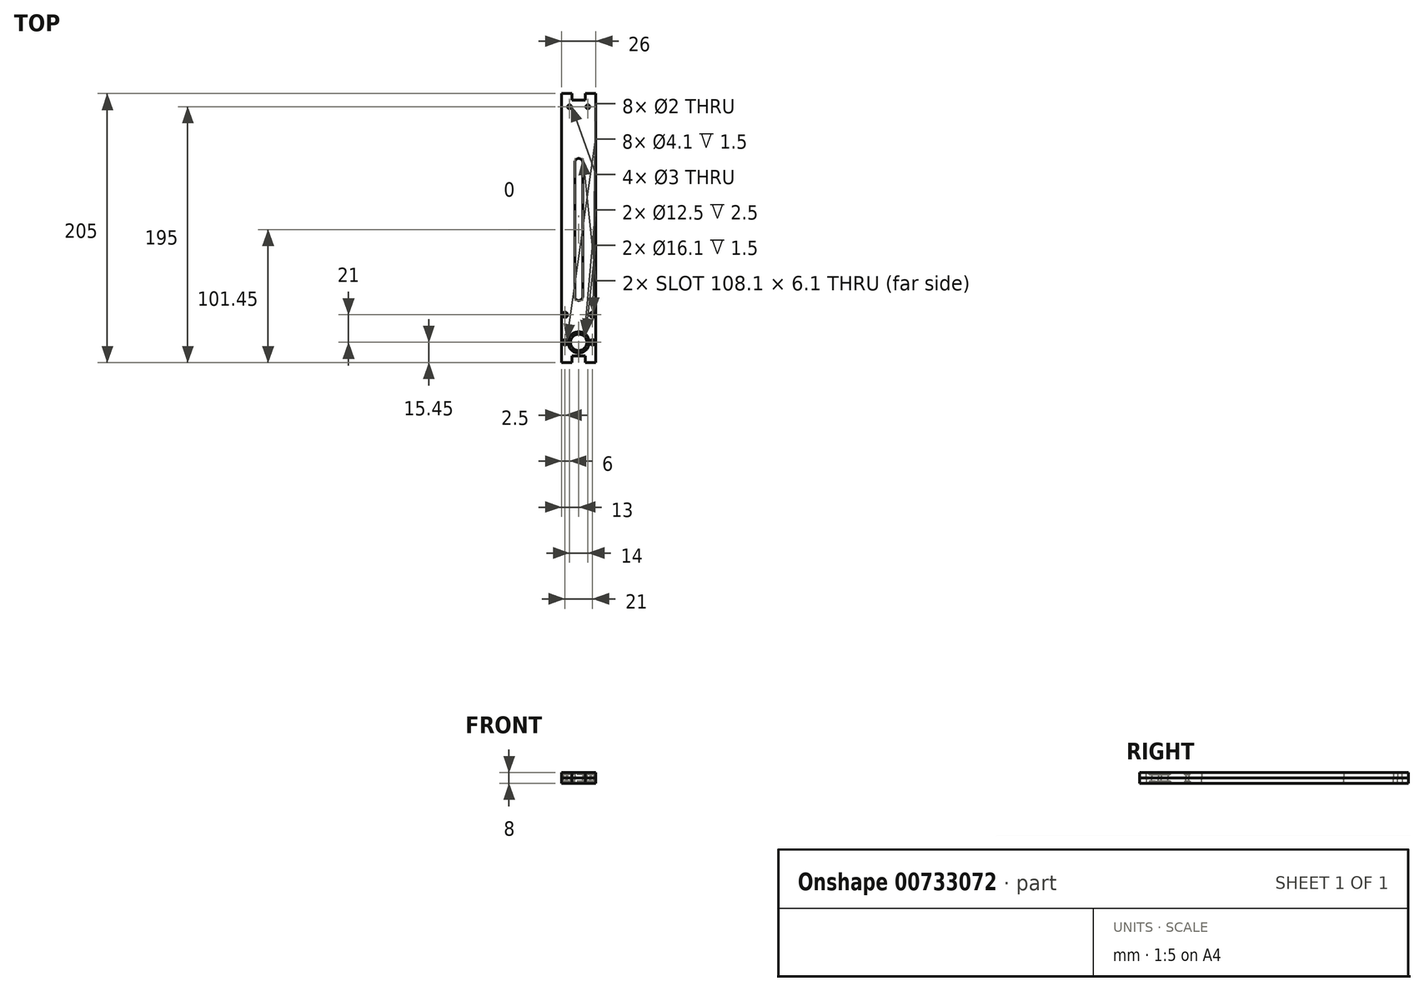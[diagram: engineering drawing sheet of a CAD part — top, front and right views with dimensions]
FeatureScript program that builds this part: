
annotation { "Feature Type Name" : "Feature", "Feature Type Description" : "" }
export const myFeature = defineFeature(function(context is Context, id is Id, definition is map)
    precondition{}
    {
        {
            var Q0;
            Q0=qCreatedBy(makeId("Top.planeOp"),FACE);
            var sketch = newSketch(context, id + "F0", { "sketchPlane" : qUnion([Q0])});
            skArc(sketch, "E0", {"start": v(3.05, 51) * mm, "mid": v(0, 54.05) * mm, "end": v(-3.05, 51) * mm});
            skArc(sketch, "E1.MirrorC", {"start": v(3.05, -51) * mm, "mid": v(0, -54.05) * mm, "end": v(-3.05, -51) * mm});
            skLineSegment(sketch, "E2", {"start": v(-3.05, 51) * mm, "end": v(-3.05, -51) * mm});
            skLineSegment(sketch, "E3.MirrorCS", {"start": v(3.05, 51) * mm, "end": v(3.05, -51) * mm});
            skCircle(sketch, "E4", {"center": v(-10.5, -65) * mm, "radius": 1 * mm});
            skCircle(sketch, "E5.MirrorC", {"center": v(10.5, -65) * mm, "radius": 1 * mm});
            skCircle(sketch, "E6", {"center": v(-10.5, -86) * mm, "radius": 1 * mm});
            skCircle(sketch, "E7.MirrorC", {"center": v(10.5, -86) * mm, "radius": 1 * mm});
            skArc(sketch, "E8", {"start": v(6.25, -86) * mm, "mid": v(0, -79.75) * mm, "end": v(-6.25, -86) * mm});
            skLineSegment(sketch, "E9", {"start": v(-6.25, -101.45) * mm, "end": v(-13, -101.45) * mm});
            skLineSegment(sketch, "E10", {"start": v(-13, -101.45) * mm, "end": v(-13, 98.55) * mm});
            skPoint(sketch, "E11", {"position": v(0, -92.25) * mm});
            skLineSegment(sketch, "E12", {"start": v(-13, 98.55) * mm, "end": v(0, 98.55) * mm});
            skLineSegment(sketch, "E13.MirrorCS", {"start": v(13, 98.55) * mm, "end": v(0, 98.55) * mm});
            skLineSegment(sketch, "E14.MirrorCS", {"start": v(13, -101.45) * mm, "end": v(13, 98.55) * mm});
            skLineSegment(sketch, "E15.MirrorCS", {"start": v(6.25, -101.45) * mm, "end": v(13, -101.45) * mm});
            skLineSegment(sketch, "E16", {"start": v(-6.25, -86) * mm, "end": v(-6.25, -101.45) * mm});
            skLineSegment(sketch, "E17.MirrorCS", {"start": v(6.25, -86) * mm, "end": v(6.25, -101.45) * mm});
            skPoint(sketch, "E18.orphan", {"position": v(0, -101.45) * mm});
            skPoint(sketch, "E19", {"position": v(0, -54.05) * mm});
            skPoint(sketch, "E20", {"position": v(0, 54.05) * mm});
            skCircle(sketch, "E21", {"center": v(-7, 93.55) * mm, "radius": 1.5 * mm});
            skCircle(sketch, "E22.MirrorC", {"center": v(7, 93.55) * mm, "radius": 1.5 * mm});
            skArc(sketch, "E23", {"start": v(-6.25, -86) * mm, "mid": v(0, -92.25) * mm, "end": v(6.25, -86) * mm});
            skLineSegment(sketch, "E24", {"start": v(-6.25, -101.45) * mm, "end": v(6.25, -101.45) * mm});
            skSolve(sketch);
        }
        {
            var Q0;
            Q0=qSketchRegion(id+"F0",true);
            extrude(context, id + "F1", {"entities" : qUnion([Q0]), "depth" : 4 * mm, "offsetDistance" : 25 * mm});
        }
        {
            var Q0;
            Q0=makeQuery(id+"F1.opExtrude","CAP_FACE",FACE,{"disambiguationData":[OSD([sQuery(id+"F0.wireOp",EDGE,"E0"),sQuery(id+"F0.wireOp",EDGE,"E1.MirrorC"),sQuery(id+"F0.wireOp",EDGE,"E2"),sQuery(id+"F0.wireOp",EDGE,"E3.MirrorCS"),sQuery(id+"F0.wireOp",EDGE,"E4"),sQuery(id+"F0.wireOp",EDGE,"E5.MirrorC"),sQuery(id+"F0.wireOp",EDGE,"E6"),sQuery(id+"F0.wireOp",EDGE,"E7.MirrorC"),sQuery(id+"F0.wireOp",EDGE,"E8"),sQuery(id+"F0.wireOp",EDGE,"E9"),sQuery(id+"F0.wireOp",EDGE,"E10"),sQuery(id+"F0.wireOp",EDGE,"E12"),sQuery(id+"F0.wireOp",EDGE,"E13.MirrorCS"),sQuery(id+"F0.wireOp",EDGE,"E14.MirrorCS"),sQuery(id+"F0.wireOp",EDGE,"E15.MirrorCS"),sQuery(id+"F0.wireOp",EDGE,"E16"),sQuery(id+"F0.wireOp",EDGE,"E17.MirrorCS")])],"isStart":false});
            var sketch = newSketch(context, id + "F2", { "sketchPlane" : qUnion([Q0])});
            skCircle(sketch, "E25", {"center": v(0, -86) * mm, "radius": 8.05 * mm});
            skCircle(sketch, "E26", {"center": v(-10.5, -86) * mm, "radius": 2.05 * mm});
            skCircle(sketch, "E27", {"center": v(-10.5, -65) * mm, "radius": 2.05 * mm});
            skCircle(sketch, "E28.MirrorC", {"center": v(10.5, -65) * mm, "radius": 2.05 * mm});
            skCircle(sketch, "E29.MirrorC", {"center": v(10.5, -86) * mm, "radius": 2.05 * mm});
            skSolve(sketch);
        }
        {
            var Q0;
            Q0=qSketchRegion(id+"F2",true);
            extrude(context, id + "F3", {"entities" : qUnion([Q0]), "operationType" : NewBodyOperationType.REMOVE, "oppositeDirection" : true, "depth" : 1.5 * mm, "offsetDistance" : 25 * mm});
        }
        {
            var Q0;
            Q0=makeQuery(id+"F1.opExtrude","CAP_FACE",FACE,{"disambiguationData":[OSD([sQuery(id+"F0.wireOp",EDGE,"E0"),sQuery(id+"F0.wireOp",EDGE,"E1.MirrorC"),sQuery(id+"F0.wireOp",EDGE,"E2"),sQuery(id+"F0.wireOp",EDGE,"E3.MirrorCS"),sQuery(id+"F0.wireOp",EDGE,"E4"),sQuery(id+"F0.wireOp",EDGE,"E5.MirrorC"),sQuery(id+"F0.wireOp",EDGE,"E6"),sQuery(id+"F0.wireOp",EDGE,"E7.MirrorC"),sQuery(id+"F0.wireOp",EDGE,"E8"),sQuery(id+"F0.wireOp",EDGE,"E9"),sQuery(id+"F0.wireOp",EDGE,"E10"),sQuery(id+"F0.wireOp",EDGE,"E12"),sQuery(id+"F0.wireOp",EDGE,"E13.MirrorCS"),sQuery(id+"F0.wireOp",EDGE,"E14.MirrorCS"),sQuery(id+"F0.wireOp",EDGE,"E15.MirrorCS"),sQuery(id+"F0.wireOp",EDGE,"E21"),sQuery(id+"F0.wireOp",EDGE,"E22.MirrorC"),sQuery(id+"F0.wireOp",EDGE,"E23"),sQuery(id+"F0.wireOp",EDGE,"E24")])],"isStart":false});
            var sketch = newSketch(context, id + "F4", { "sketchPlane" : qUnion([Q0])});
            skLineSegment(sketch, "E30", {"start": v(-13, -96.45) * mm, "end": v(13, -96.45) * mm});
            skLineSegment(sketch, "E31", {"start": v(-5, -96.45) * mm, "end": v(-5, -101.45) * mm});
            skLineSegment(sketch, "E32.MirrorCS", {"start": v(5, -96.45) * mm, "end": v(5, -101.45) * mm});
            skSolve(sketch);
        }
        {
            var Q0;
            {var subQ0=sQuery(id+"F4.wireOp",EDGE,"E31");Q0=makeQuery(id+"F4.imprint","IMPRINT",FACE,{"disambiguationData":[TD([[makeQuery(id+"F4.imprint","IMPRINT",EDGE,{"derivedFrom":subQ0}),1.0]])]});}
            extrude(context, id + "F5", {"entities" : qUnion([Q0]), "operationType" : NewBodyOperationType.REMOVE, "endBound" : BoundingType.THROUGH_ALL, "oppositeDirection" : true, "depth" : 25 * mm, "offsetDistance" : 25 * mm});
        }
        {
            var Q0;
            Q0=makeQuery(id+"F1.opExtrude","CAP_FACE",FACE,{"disambiguationData":[OSD([sQuery(id+"F0.wireOp",EDGE,"E0"),sQuery(id+"F0.wireOp",EDGE,"E1.MirrorC"),sQuery(id+"F0.wireOp",EDGE,"E2"),sQuery(id+"F0.wireOp",EDGE,"E3.MirrorCS"),sQuery(id+"F0.wireOp",EDGE,"E4"),sQuery(id+"F0.wireOp",EDGE,"E5.MirrorC"),sQuery(id+"F0.wireOp",EDGE,"E6"),sQuery(id+"F0.wireOp",EDGE,"E7.MirrorC"),sQuery(id+"F0.wireOp",EDGE,"E8"),sQuery(id+"F0.wireOp",EDGE,"E9"),sQuery(id+"F0.wireOp",EDGE,"E10"),sQuery(id+"F0.wireOp",EDGE,"E12"),sQuery(id+"F0.wireOp",EDGE,"E13.MirrorCS"),sQuery(id+"F0.wireOp",EDGE,"E14.MirrorCS"),sQuery(id+"F0.wireOp",EDGE,"E15.MirrorCS"),sQuery(id+"F0.wireOp",EDGE,"E21"),sQuery(id+"F0.wireOp",EDGE,"E22.MirrorC"),sQuery(id+"F0.wireOp",EDGE,"E23"),sQuery(id+"F0.wireOp",EDGE,"E24")])],"isStart":false});
            var sketch = newSketch(context, id + "F6", { "sketchPlane" : qUnion([Q0])});
            skLineSegment(sketch, "E33", {"start": v(-13, 98.55) * mm, "end": v(-13, 103.55) * mm});
            skLineSegment(sketch, "E34", {"start": v(-13, 103.55) * mm, "end": v(-5, 103.55) * mm});
            skLineSegment(sketch, "E35", {"start": v(-5, 103.55) * mm, "end": v(-5, 98.55) * mm});
            skLineSegment(sketch, "E36", {"start": v(-5, 98.55) * mm, "end": v(-13, 98.55) * mm});
            skLineSegment(sketch, "E37.MirrorCS", {"start": v(13, 103.55) * mm, "end": v(5, 103.55) * mm});
            skLineSegment(sketch, "E38.MirrorCS", {"start": v(13, 98.55) * mm, "end": v(13, 103.55) * mm});
            skLineSegment(sketch, "E39.MirrorCS", {"start": v(5, 103.55) * mm, "end": v(5, 98.55) * mm});
            skLineSegment(sketch, "E40.MirrorCS", {"start": v(5, 98.55) * mm, "end": v(13, 98.55) * mm});
            skSolve(sketch);
        }
        {
            var Q0;
            Q0=qSketchRegion(id+"F6",true);
            extrude(context, id + "F7", {"entities" : qUnion([Q0]), "operationType" : NewBodyOperationType.ADD, "oppositeDirection" : true, "depth" : 4 * mm, "offsetDistance" : 25 * mm});
        }
        {
            var Q0;
            Q0=makeQuery(id+"F1.opExtrude","SWEPT_BODY",BODY,{"disambiguationData":[OSD([sQuery(id+"F0.wireOp",EDGE,"E0"),sQuery(id+"F0.wireOp",EDGE,"E1.MirrorC"),sQuery(id+"F0.wireOp",EDGE,"E2"),sQuery(id+"F0.wireOp",EDGE,"E3.MirrorCS"),sQuery(id+"F0.wireOp",EDGE,"E4"),sQuery(id+"F0.wireOp",EDGE,"E5.MirrorC"),sQuery(id+"F0.wireOp",EDGE,"E6"),sQuery(id+"F0.wireOp",EDGE,"E7.MirrorC"),sQuery(id+"F0.wireOp",EDGE,"E8"),sQuery(id+"F0.wireOp",EDGE,"E9"),sQuery(id+"F0.wireOp",EDGE,"E10"),sQuery(id+"F0.wireOp",EDGE,"E12"),sQuery(id+"F0.wireOp",EDGE,"E13.MirrorCS"),sQuery(id+"F0.wireOp",EDGE,"E14.MirrorCS"),sQuery(id+"F0.wireOp",EDGE,"E15.MirrorCS"),sQuery(id+"F0.wireOp",EDGE,"E21"),sQuery(id+"F0.wireOp",EDGE,"E22.MirrorC"),sQuery(id+"F0.wireOp",EDGE,"E23"),sQuery(id+"F0.wireOp",EDGE,"E24")])]});
            var Q1;
            Q1=qCreatedBy(makeId("Top.planeOp"),FACE);
            mirror(context, id + "F8", {"entities" : qUnion([Q0]), "mirrorPlane" : qUnion([Q1])});
        }
    });
